# Revit family: RN 92044 Optifitt-Serra-Winkelverschraubung
name_source: partatom
category: Rohrformteile
units: mm (PartAtom-declared; Revit-internal decimal feet)

## family parameters
Arbeitsebenenbasiert = Nein
Beim Laden mit Abzugskörper schneiden = Nein
Bemaßung runder Anschluss = Durchmesser verwenden
Gemeinsam genutzt = Nein
Immer vertikal = Ja
Teiletyp = Verbindung

## types (6) — shared parameters
1.010.00.2 Blattnummer der Richtlinie = 29
1.010.00.3 Ausgabedatum (Monat) der Richtlinie = 201308
1.010.00.4 Herstellername = R. Nussbaum AG
1.010.00.5 Revisionsdatum der Datei = 20190521
1.010.00.6 Webadresse des Herstellers = http://www.nussbaum.ch
1.100.00.4 Produktbezeichnung = Versorgung
1.110.00.2 Index = 3
1.110.00.4 Produktbezeichnung = Optifitt-Serra
1.960/3L.00.8 Link (URL) = https://www.nussbaum.ch
29.700.00.4 Produktname = Optifitt-Serra-Winkelverschraubung
29.700.00.5 Produktkennung = 2
29.700.00.6 Querschnittsform = 1
29.700.00.7 Nennweitensystem = DN
29.700.00.8 Nenndrucksystem = PN
29.710.02.4 Nenndruck = 16
29.710.02.5 max. zul. Überdruck [hPa] = 1600
29.710.02.7 max. zul. Dauer-Betriebsdruck [hPa] = 1600
29.710.02.9 max. zul. Dauer-Betriebstemperatur [°C] = 90
Connector Visibility = Nein
EnclosingSpace Visibility = Nein
Hersteller = R. Nussbaum AG
URL = https://www.nussbaum.ch

## per-type parameters (varying)
| type | 1.800.00.3 TGA-Nummer | 1.800.00.4 Kommentarfeld | 1.810.00.3 Hersteller-Bestellnummer | 1.810.00.4 DATANORM-Nummer | 1.810.00.5 StLB-Nummer | 1.810.00.6 GTIN-Nummer | 29.710.02.10 Formstück-Gewicht [kg] | 29.710.02.3 Benennung | CONNECTOR0_DIAMETER_dZ_0r | CONNECTOR0_dZ_01 | CONNECTOR0_ref_dZ | CONNECTOR1_DIAMETER_dX_0r | CONNECTOR1_dX_00 | CONNECTOR1_dX_01 | CONNECTOR1_ref_dX | CONNECTOR1_ref_dZ | Modell | R. Nussbaum AG 92044.04 de Visibility | R. Nussbaum AG 92044.05 de Visibility | R. Nussbaum AG 92044.06 de Visibility | R. Nussbaum AG 92044.07 de Visibility | R. Nussbaum AG 92044.08 de Visibility | R. Nussbaum AG 92044.09 de Visibility | Typenkommentare |
| DN=50 | 01900300000000000000000000000000000000000000000043000000000000000006 | 92044.09, Optifitt-Serra-Winkelverschraubung, DN=50, L=69, R=2, Rp=2 | 92044.09 | 92044.09 | 215.457 | 7612945038159 | 1.36 | Optifitt-Serra-Winkelverschraubung, DN=50, L=69, R=2, Rp=2 | 50 mm | 24 mm  [stored 0.0787402 ft] | 24 mm  [stored 0.0787402 ft] | 50 mm | 69 mm | 45 mm | 45 mm | 112 mm | 92044.09 | Nein | Nein | Nein | Nein | Nein | Ja | Optifitt-Serra-Winkelverschraubung  DN=50 |
| DN=40 | 01900300000000000000000000000000000000000000000043000000000000000005 | 92044.08, Optifitt-Serra-Winkelverschraubung, DN=40, L=59, R=1½, Rp=1½ | 92044.08 | 92044.08 | 215.456 | 7612945038142 | 0.78 | Optifitt-Serra-Winkelverschraubung, DN=40, L=59, R=1½, Rp=1½ | 40 mm | 19 mm | 19 mm | 40 mm | 59 mm | 40 mm | 40 mm | 95 mm | 92044.08 | Nein | Nein | Nein | Nein | Ja | Nein | Optifitt-Serra-Winkelverschraubung  DN=40 |
| DN=32 | 01900300000000000000000000000000000000000000000043000000000000000004 | 92044.07, Optifitt-Serra-Winkelverschraubung, DN=32, L=57, R=1¼, Rp=1¼ | 92044.07 | 92044.07 | 215.455 | 7612945038135 | 0.56 | Optifitt-Serra-Winkelverschraubung, DN=32, L=57, R=1¼, Rp=1¼ | 32 mm | 19 mm | 19 mm | 32 mm | 57 mm | 38 mm | 38 mm | 83 mm | 92044.07 | Nein | Nein | Nein | Ja | Nein | Nein | Optifitt-Serra-Winkelverschraubung  DN=32 |
| DN=25 | 01900300000000000000000000000000000000000000000043000000000000000003 | 92044.06, Optifitt-Serra-Winkelverschraubung, DN=25, L=47, R=1, Rp=1 | 92044.06 | 92044.06 | 215.454 | 7612945038128 | 0.425 | Optifitt-Serra-Winkelverschraubung, DN=25, L=47, R=1, Rp=1 | 25 mm  [stored 0.082021 ft] | 17 mm | 17 mm | 25 mm  [stored 0.082021 ft] | 47 mm | 30 mm | 30 mm | 77 mm | 92044.06 | Nein | Nein | Ja | Nein | Nein | Nein | Optifitt-Serra-Winkelverschraubung  DN=25 |
| DN=20 | 01900300000000000000000000000000000000000000000043000000000000000002 | 92044.05, Optifitt-Serra-Winkelverschraubung, DN=20, L=39, R=¾, Rp=¾ | 92044.05 | 92044.05 | 215.453 | 7612945038111 | 0.264 | Optifitt-Serra-Winkelverschraubung, DN=20, L=39, R=¾, Rp=¾ | 20 mm | 15 mm | 15 mm | 20 mm | 39 mm | 24 mm  [stored 0.0787402 ft] | 24 mm  [stored 0.0787402 ft] | 65 mm | 92044.05 | Nein | Ja | Nein | Nein | Nein | Nein | Optifitt-Serra-Winkelverschraubung  DN=20 |
| DN=15 | 01900300000000000000000000000000000000000000000043000000000000000001 | 92044.04, Optifitt-Serra-Winkelverschraubung, DN=15, L=33, R=½, Rp=½ | 92044.04 | 92044.04 | 215.452 | 7612945038104 | 0.171 | Optifitt-Serra-Winkelverschraubung, DN=15, L=33, R=½, Rp=½ | 15 mm | 13 mm | 13 mm | 15 mm | 33 mm | 20 mm | 20 mm | 57 mm | 92044.04 | Ja | Nein | Nein | Nein | Nein | Nein | Optifitt-Serra-Winkelverschraubung  DN=15 |

note: [stored X ft] marks values corroborated as IEEE doubles in the binary element streams (Revit-internal decimal feet)

## geometry (parser evidence)
native form markers: Sweep x2
no freeform markers — native parametric forms only
